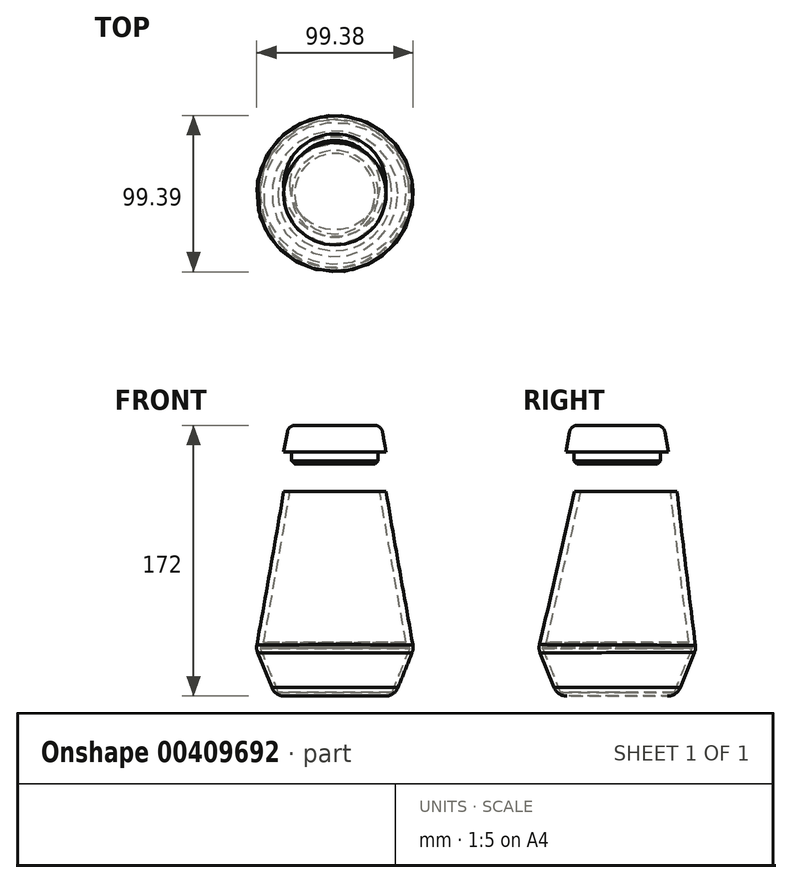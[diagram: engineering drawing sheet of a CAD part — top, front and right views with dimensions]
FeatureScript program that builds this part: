
annotation { "Feature Type Name" : "Feature", "Feature Type Description" : "" }
export const myFeature = defineFeature(function(context is Context, id is Id, definition is map)
    precondition{}
    {
        {
            var Q0;
            Q0=qCreatedBy(makeId("Top.planeOp"),FACE);
            cPlane(context, id + "F0", {"entities" : qUnion([Q0]), "cplaneType" : CPlaneType.OFFSET, "offset" : 100 * mm, "width" : 152.4 * mm, "height" : 152.4 * mm});
        }
        {
            var Q0;
            Q0=qCreatedBy(makeId("Top.planeOp"),FACE);
            var sketch = newSketch(context, id + "F1", { "sketchPlane" : qUnion([Q0])});
            skCircle(sketch, "E0", {"center": v(0, 0) * mm, "radius": 50 * mm});
            skSolve(sketch);
        }
        {
            var Q0;
            Q0=qCreatedBy(id+"F0.planeOp",FACE);
            var sketch = newSketch(context, id + "F2", { "sketchPlane" : qUnion([Q0])});
            skCircle(sketch, "E1", {"center": v(0, 5.49) * mm, "radius": 32.5 * mm});
            skSolve(sketch);
        }
        {
            var Q0;
            Q0=makeQuery(id+"F2.imprint","IMPRINT",FACE,{"disambiguationData":[TD([[makeQuery(id+"F2.imprint","IMPRINT",EDGE,{"derivedFrom":sQuery(id+"F2.wireOp",EDGE,"E1")}),1.0]])]});
            var Q1;
            Q1=makeQuery(id+"F1.imprint","IMPRINT",FACE,{"disambiguationData":[TD([[makeQuery(id+"F1.imprint","IMPRINT",EDGE,{"derivedFrom":sQuery(id+"F1.wireOp",EDGE,"E0")}),1.0]])]});
            loft(context, id + "F3", {"sheetProfilesArray" : [{ "sheetProfileEntities" : qUnion([Q0]) }, { "sheetProfileEntities" : qUnion([Q1]) }]});
        }
        {
            var Q0;
            Q0=makeQuery(id+"F3.opLoft","CAP_FACE",FACE,{"disambiguationData":[OSD([makeQuery(id+"F2.imprint","IMPRINT",FACE,{"disambiguationData":[TD([[makeQuery(id+"F2.imprint","IMPRINT",EDGE,{"derivedFrom":sQuery(id+"F2.wireOp",EDGE,"E1")}),1.0]])]})])],"isStart":true});
            shell(context, id + "F4", {"entities" : qUnion([Q0]), "thickness" : 4 * mm});
        }
        {
            var Q0;
            Q0=qCreatedBy(makeId("Top.planeOp"),FACE);
            cPlane(context, id + "F5", {"entities" : qUnion([Q0]), "cplaneType" : CPlaneType.OFFSET, "offset" : 30 * mm, "oppositeDirection" : true, "width" : 150 * mm, "height" : 150 * mm});
        }
        {
            var Q0;
            Q0=qCreatedBy(id+"F5.planeOp",FACE);
            var sketch = newSketch(context, id + "F6", { "sketchPlane" : qUnion([Q0])});
            skCircle(sketch, "E2", {"center": v(0, 0) * mm, "radius": 37.84 * mm});
            skSolve(sketch);
        }
        {
            var Q1;
            Q1=makeQuery(id+"F6.imprint","IMPRINT",FACE,{"disambiguationData":[TD([[makeQuery(id+"F6.imprint","IMPRINT",EDGE,{"derivedFrom":sQuery(id+"F6.wireOp",EDGE,"E2")}),1.0]])]});
            var Q2;
            Q2=makeQuery(id+"F3.opLoft","CAP_FACE",FACE,{"disambiguationData":[OSD([makeQuery(id+"F1.imprint","IMPRINT",FACE,{"disambiguationData":[TD([[makeQuery(id+"F1.imprint","IMPRINT",EDGE,{"derivedFrom":sQuery(id+"F1.wireOp",EDGE,"E0")}),1.0]])]})])],"isStart":true});
            loft(context, id + "F7", {"operationType" : NewBodyOperationType.ADD, "sheetProfilesArray" : [{ "sheetProfileEntities" : qUnion([Q1]) }, { "sheetProfileEntities" : qUnion([Q2]) }]});
        }
        {
            var Q0;
            Q0=makeQuery(id+"F7.opLoft","CAP_FACE",FACE,{"disambiguationData":[OSD([makeQuery(id+"F6.imprint","IMPRINT",FACE,{"disambiguationData":[TD([[makeQuery(id+"F6.imprint","IMPRINT",EDGE,{"derivedFrom":sQuery(id+"F6.wireOp",EDGE,"E2")}),1.0]])]})])],"isStart":true});
            var Q1;
            Q1=makeQuery(id+"F3.opLoft","SWEPT_BODY",BODY,{"disambiguationData":[OSD([makeQuery(id+"F1.imprint","IMPRINT",FACE,{"disambiguationData":[TD([[makeQuery(id+"F1.imprint","IMPRINT",EDGE,{"derivedFrom":sQuery(id+"F1.wireOp",EDGE,"E0")}),1.0]])]}),makeQuery(id+"F2.imprint","IMPRINT",FACE,{"disambiguationData":[TD([[makeQuery(id+"F2.imprint","IMPRINT",EDGE,{"derivedFrom":sQuery(id+"F2.wireOp",EDGE,"E1")}),1.0]])]})])]});
            shell(context, id + "F8", {"isHollow" : true, "entities" : qUnion([Q0]), "parts" : qUnion([Q1]), "thickness" : 2.5 * mm});
        }
        {
            var Q0;
            Q0=qCreatedBy(id+"F0.planeOp",FACE);
            cPlane(context, id + "F9", {"entities" : qUnion([Q0]), "cplaneType" : CPlaneType.OFFSET, "offset" : 25 * mm, "width" : 150 * mm, "height" : 150 * mm});
        }
        {
            var Q0;
            Q0=qCreatedBy(id+"F9.planeOp",FACE);
            var sketch = newSketch(context, id + "F10", { "sketchPlane" : qUnion([Q0])});
            skCircle(sketch, "E3", {"center": v(0, 0) * mm, "radius": 32.5 * mm});
            skSolve(sketch);
        }
        {
            var Q0;
            Q0=qCreatedBy(id+"F9.planeOp",FACE);
            cPlane(context, id + "F11", {"entities" : qUnion([Q0]), "cplaneType" : CPlaneType.OFFSET, "offset" : 17 * mm, "width" : 150 * mm, "height" : 150 * mm});
        }
        {
            var Q0;
            Q0=qCreatedBy(id+"F11.planeOp",FACE);
            var sketch = newSketch(context, id + "F12", { "sketchPlane" : qUnion([Q0])});
            skCircle(sketch, "E4", {"center": v(0, 0) * mm, "radius": 29.5 * mm});
            skSolve(sketch);
        }
        {
            var Q0;
            Q0=makeQuery(id+"F12.imprint","IMPRINT",FACE,{"disambiguationData":[TD([[makeQuery(id+"F12.imprint","IMPRINT",EDGE,{"derivedFrom":sQuery(id+"F12.wireOp",EDGE,"E4")}),1.0]])]});
            var Q1;
            Q1=makeQuery(id+"F10.imprint","IMPRINT",FACE,{"disambiguationData":[TD([[makeQuery(id+"F10.imprint","IMPRINT",EDGE,{"derivedFrom":sQuery(id+"F10.wireOp",EDGE,"E3")}),1.0]])]});
            loft(context, id + "F13", {"sheetProfilesArray" : [{ "sheetProfileEntities" : qUnion([Q0]) }, { "sheetProfileEntities" : qUnion([Q1]) }]});
        }
        {
            var Q0;
            Q0=makeQuery(id+"F13.opLoft","CAP_FACE",FACE,{"disambiguationData":[OSD([makeQuery(id+"F10.imprint","IMPRINT",FACE,{"disambiguationData":[TD([[makeQuery(id+"F10.imprint","IMPRINT",EDGE,{"derivedFrom":sQuery(id+"F10.wireOp",EDGE,"E3")}),1.0]])]})])],"isStart":true});
            var sketch = newSketch(context, id + "F14", { "sketchPlane" : qUnion([Q0])});
            skCircle(sketch, "E5", {"center": v(0, 0) * mm, "radius": 27.5 * mm});
            skSolve(sketch);
        }
        {
            var Q0;
            Q0=makeQuery(id+"F14.imprint","IMPRINT",FACE,{"disambiguationData":[TD([[makeQuery(id+"F14.imprint","IMPRINT",EDGE,{"derivedFrom":sQuery(id+"F14.wireOp",EDGE,"E5")}),1.0]])]});
            var sketch = newSketch(context, id + "F15", { "sketchPlane" : qUnion([Q0])});
            skSolve(sketch);
        }
        {
            var Q0;
            Q0=qSketchRegion(id+"F15",true);
            var Q1;
            Q1=makeQuery(id+"F14.imprint","IMPRINT",FACE,{"disambiguationData":[TD([[makeQuery(id+"F14.imprint","IMPRINT",EDGE,{"derivedFrom":sQuery(id+"F14.wireOp",EDGE,"E5")}),1.0]])]});
            extrude(context, id + "F16", {"entities" : qUnion([Q0, Q1]), "operationType" : NewBodyOperationType.ADD, "depth" : 7.5 * mm});
        }
        {
            var Q0;
            {var subQ0=sQuery(id+"F2.wireOp",EDGE,"E1");var subQ1=sQuery(id+"F1.wireOp",EDGE,"E0");Q0=makeQuery(id+"F7.boolean.opBoolean","MERGE",EDGE,{"derivedFrom":[makeQuery(id+"F3.opLoft","MID_CAP_EDGE",EDGE,{"disambiguationData":[OSD([subQ1,subQ0])],"capPos":1.0}),makeQuery(id+"F7.opLoft","MID_CAP_EDGE",EDGE,{"disambiguationData":[OSD([subQ1,subQ0,sQuery(id+"F6.wireOp",EDGE,"E2")])],"capPos":1.0})]});}
            var Q1;
            Q1=makeQuery(id+"F7.opLoft","MID_CAP_EDGE",EDGE,{"disambiguationData":[OSD([sQuery(id+"F6.wireOp",EDGE,"E2")])],"capPos":0.0});
            fillet(context, id + "F17", {"entities" : qUnion([Q0, Q1]), "radius" : 8.77 * mm, "tangentPropagation" : true, "allowEdgeOverflow" : false});
        }
        {
            var Q0;
            Q0=makeQuery(id+"F13.opLoft","MID_CAP_EDGE",EDGE,{"disambiguationData":[OSD([sQuery(id+"F12.wireOp",EDGE,"E4")])],"capPos":0.0});
            fillet(context, id + "F18", {"entities" : qUnion([Q0]), "radius" : 5 * mm, "tangentPropagation" : true, "allowEdgeOverflow" : false});
        }
        {
            var Q0;
            Q0=makeQuery(id+"F16.opExtrude","CAP_EDGE",EDGE,{"disambiguationData":[OSD([sQuery(id+"F14.wireOp",EDGE,"E5")])],"isStart":false});
            chamfer(context, id + "F19", {"entities" : qUnion([Q0]), "width" : 2 * mm, "tangentPropagation" : true});
        }
    });
